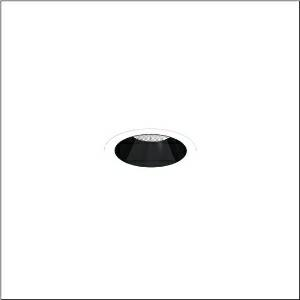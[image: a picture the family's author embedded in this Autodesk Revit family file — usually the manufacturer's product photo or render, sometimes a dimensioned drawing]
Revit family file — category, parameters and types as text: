
# Revit family: lunis_21_m_51db17tc91c
name_source: partatom
category: Lighting Fixtures
units: mm (PartAtom-declared; Revit-internal decimal feet)

## family parameters
Cut with Voids When Loaded = No
Host = Face
Light Source = No
Part Type = Normal
Room Calculation Point = No
Round Connector Dimension = Use Diameter
Shared = No

## types (1)
- --- (1 x LED 3000 K ... 6500 K, 3340 lm, 26 W, 4000K)
    Apparent Load = 26 VA
    CIE Flux Codes = 98 100 100 100 100
    Color Rendering = 80
    Color Temperature = 4000K
    Default Elevation = 1800 mm
    Description = Lunis 21,  M, downlight, light control with lens, of PMMA, anti glare with reflector, of aluminium, light emission: direct distribution, LED rated luminous flux: 3.340lm, light colour: 8tw, with terminal, 5-pole, mains connection: 220..240V, AC/DC, 0/50..60Hz, housing, round, of diecast aluminium, traffic white (RAL 9016), diameter: 115mm, clamping range: 1..40mm, protection rating (complete): IP20, protection rating (on room side): IP54, insulation class (complete): insulation class II (safety insulation), certification: CE, impact resistance: IK03, packaging unit: 1 piece
    Height = 0 mm  [stored 0 ft]
    Lamp = 1 x LED 3000 K ... 6500 K
    Lamp Light Flux = 3340 lm
    Lamp Power = 26 W
    Lamp count = 1
    Length = 115 mm
    Luminous efficacy = 128 lm/W
    Manufacturer = Siteco
    ModVariant = No
    Model = 51DB17TC91C
    Mounting Place = Ceiling
    Mounting Type = Recessed
    Number of Poles = 1
    OnlyDefault = Yes
    Power Factor = 1
    Product Name = Lunis 21 M
    Product group = downlight
    ProductGroupID = 400
    Protection Class = Protection class II
    Protection Degree = IP 20
    RLX_Detail_Level = 1
    RLX_Emergency_Light_Flux = 0 lm
    RLX_Emergency_Type = 0
    RLX_Emergency_Type_DB = No
    RlxData = <blob elided: 11409 chars, md5=d1568408>
    Socket = socket
    Standby Power = 0 W
    System Light Flux = 3340 lm
    System Power = 26 W
    Type Comments = individual setting: CCT=4000K, colour temperature 4000K, luminous flux: 100 % | (ON | ON | OFF | OFF) | 700 mA
    Type Image = l_1290854.jpg
    URL = http://relux.com
    VarID = @adj_020028
    Voltage = 0 V
    Weight = 0.00 kg
    Width = 0 mm  [stored 0 ft]

note: [stored X ft] marks values corroborated as IEEE doubles in the binary element streams (Revit-internal decimal feet)

## geometry (parser evidence)
native form markers: Sweep x11
no freeform markers — native parametric forms only
